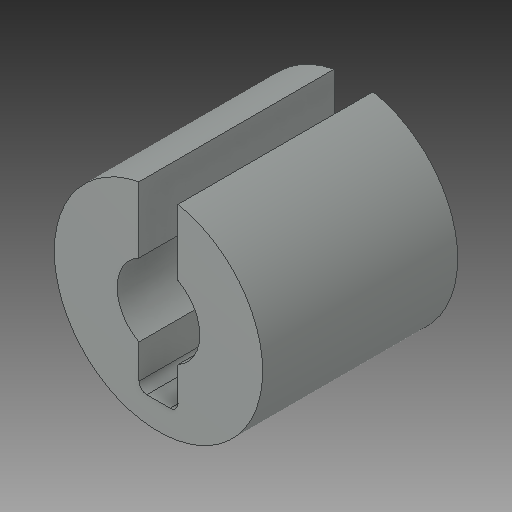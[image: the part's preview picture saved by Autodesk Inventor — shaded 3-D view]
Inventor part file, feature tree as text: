
AUTODESK INVENTOR PART (.ipt)
format: ipt  version: 2017 SP1 (Build 210196100, 196)  size: 111,616 bytes
history: native  units: in
note: dims shown in document units (in); Inventor stores cm internally (conversion verified against a paired STEP export)
features: fillet x1
ambient origin geometry x8: Origin, YZ Plane, XZ Plane, XY Plane, X Axis, Y Axis, Z Axis, Center Point
bodies: Solid1 (feature_tree)
feature tree (1):
  fillet  "Fillet1"  [1 undecoded]
note: 1 required parameter value undecoded (feature->parameter linkage not recoverable at this tier; creation-order binding heuristic only, values carry confidence <= 0.55)
